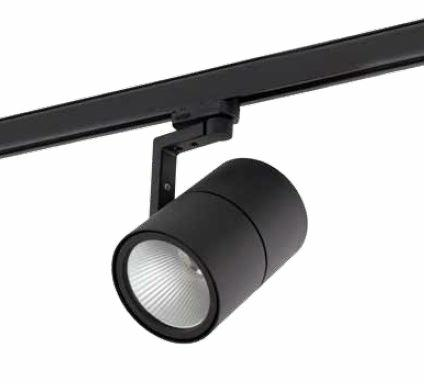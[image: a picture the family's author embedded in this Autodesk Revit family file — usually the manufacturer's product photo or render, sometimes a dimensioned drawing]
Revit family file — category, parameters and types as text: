
# Revit family: DS 1011 PLN (Ra80)
name_source: partatom
category: Lighting Fixtures
revit_build: Autodesk Revit 2017 (Build: 20160225_1515(x64)
units: mm (PartAtom-declared; Revit-internal decimal feet)

## family parameters
Cut with Voids When Loaded = No
Host = Face
Light Source = Yes
Part Type = Normal
Room Calculation Point = No
Round Connector Dimension = Use Diameter
Shared = No

## types (18) — shared parameters
Color Filter = 16777215
Default Elevation = 1219 mm
Dimming Lamp Color Temperature Shift = <None>
Emit Shape Visible in Rendering = Yes
Emit from Circle Diameter = 100 mm  [stored 0.328084 ft]
Light Source Symbol Length = 3048 mm  [stored 10 ft]
Manufacturer = ARLIGHT
Spot Field Angle = 90.00°
Tilt Angle = 90.00°
Type Image = DS 1011 PLN.JPG

## per-type parameters (varying)
| type | Spot Beam Angle | Wattage Comments |
| DSPLN.11.19.30.15.80 | 15.00° | 19 |
| DSPLN.11.19.40.15.80 | 15.00° | 19 |
| DSPLN.11.19.30.24.80 | 24.00° | 19 |
| DSPLN.11.19.40.24.80 | 24.00° | 19 |
| DSPLN.11.19.30.42.80 | 42.00° | 19 |
| DSPLN.11.19.40.42.80 | 42.00° | 19 |
| DSPLN.11.27.30.15.80 | 15.00° | 27 |
| DSPLN.11.27.40.15.80 | 15.00° | 27 |
| DSPLN.11.27.30.24.80 | 24.00° | 27 |
| DSPLN.11.27.40.24.80 | 24.00° | 27 |
| DSPLN.11.27.30.42.80 | 42.00° | 27 |
| DSPLN.11.27.40.42.80 | 42.00° | 27 |
| DSPLN.11.35.30.15.80 | 15.00° | 35 |
| DSPLN.11.35.40.15.80 | 15.00° | 35 |
| DSPLN.11.35.30.24.80 | 24.00° | 35 |
| DSPLN.11.35.40.24.80 | 24.00° | 35 |
| DSPLN.11.35.30.42.80 | 42.00° | 35 |
| DSPLN.11.35.40.42.80 | 42.00° | 35 |

note: [stored X ft] marks values corroborated as IEEE doubles in the binary element streams (Revit-internal decimal feet)

## geometry (parser evidence)
native form markers: Sweep x3
no freeform markers — native parametric forms only
